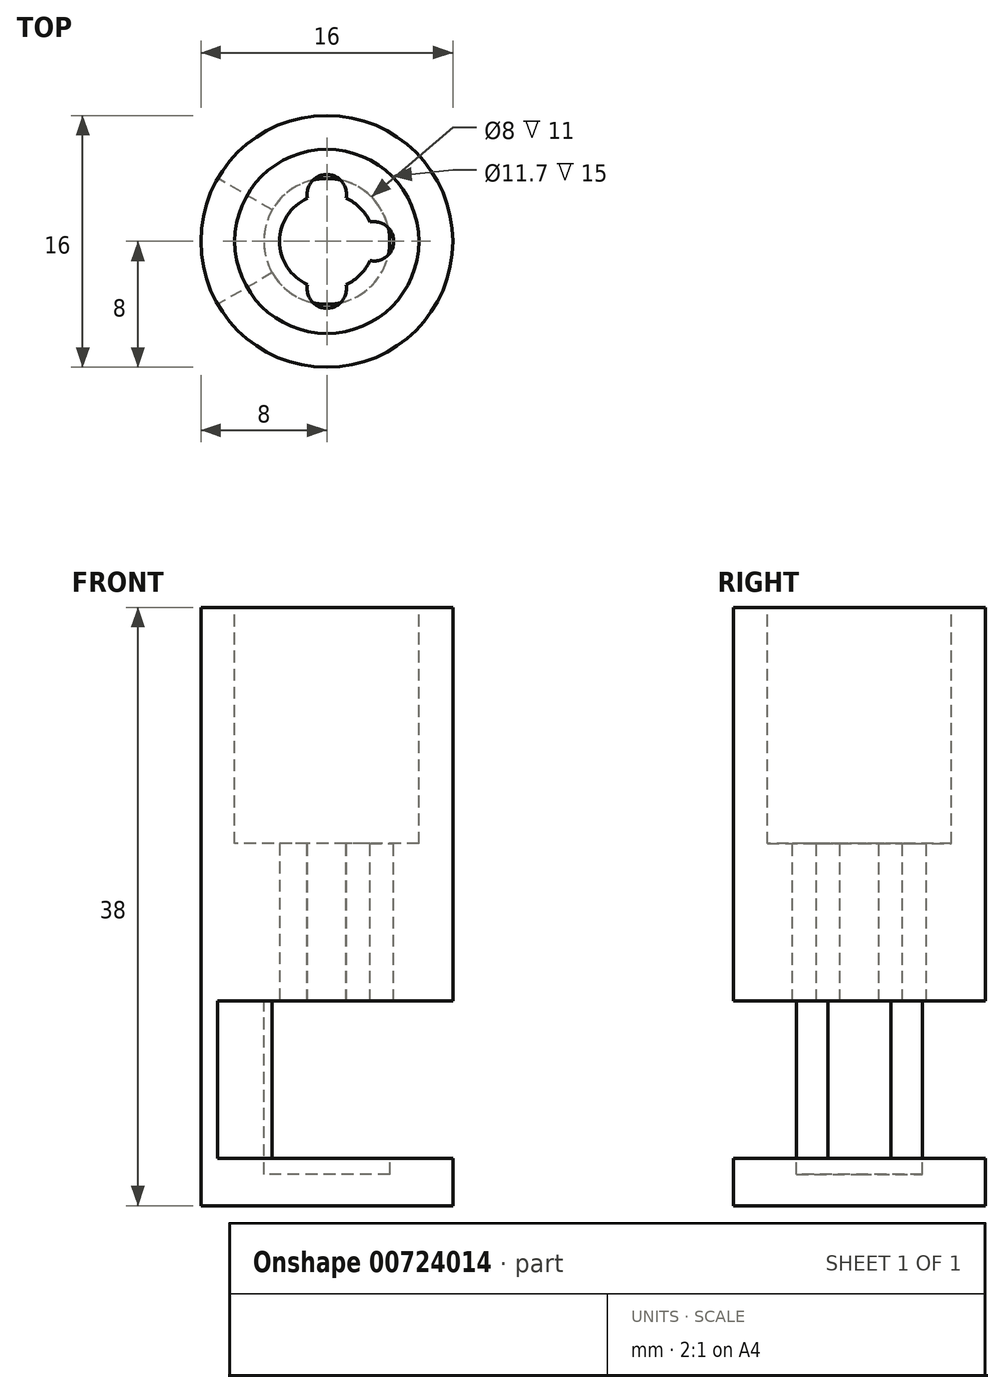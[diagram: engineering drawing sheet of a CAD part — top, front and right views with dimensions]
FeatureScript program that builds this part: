
annotation { "Feature Type Name" : "Feature", "Feature Type Description" : "" }
export const myFeature = defineFeature(function(context is Context, id is Id, definition is map)
    precondition{}
    {
        {
            var Q0;
            Q0=qCreatedBy(makeId("Top.planeOp"),FACE);
            var sketch = newSketch(context, id + "F0", { "sketchPlane" : qUnion([Q0])});
            skCircle(sketch, "E0", {"center": v(0, 0) * mm, "radius": 8 * mm});
            skSolve(sketch);
        }
        {
            var Q0;
            Q0=makeQuery(id+"F0.imprint","IMPRINT",FACE,{"disambiguationData":[TD([[makeQuery(id+"F0.imprint","IMPRINT",EDGE,{"derivedFrom":sQuery(id+"F0.wireOp",EDGE,"E0")}),1.0]])]});
            extrude(context, id + "F1", {"entities" : qUnion([Q0]), "depth" : 3 * mm, "offsetDistance" : 25 * mm});
        }
        {
            var Q0;
            Q0=makeQuery(id+"F1.opExtrude","CAP_FACE",FACE,{"disambiguationData":[OSD([sQuery(id+"F0.wireOp",EDGE,"E0")])],"isStart":false});
            var sketch = newSketch(context, id + "F2", { "sketchPlane" : qUnion([Q0])});
            skCircle(sketch, "E1", {"center": v(0, 0) * mm, "radius": 4 * mm});
            skSolve(sketch);
        }
        {
            var Q0;
            Q0=makeQuery(id+"F2.imprint","IMPRINT",FACE,{"disambiguationData":[TD([[makeQuery(id+"F2.imprint","IMPRINT",EDGE,{"derivedFrom":sQuery(id+"F2.wireOp",EDGE,"E1")}),1.0]])]});
            extrude(context, id + "F3", {"entities" : qUnion([Q0]), "operationType" : NewBodyOperationType.REMOVE, "oppositeDirection" : true, "depth" : 1 * mm, "offsetDistance" : 25 * mm});
        }
        {
            var Q0;
            Q0=makeQuery(id+"F1.opExtrude","CAP_FACE",FACE,{"disambiguationData":[OSD([sQuery(id+"F0.wireOp",EDGE,"E0")])],"isStart":false});
            var sketch = newSketch(context, id + "F4", { "sketchPlane" : qUnion([Q0])});
            skArc(sketch, "E2", {"start": v(-6.93, 4) * mm, "mid": v(-8, 0) * mm, "end": v(-6.93, -4) * mm});
            skLineSegment(sketch, "E3", {"start": v(-3.46, 2) * mm, "end": v(-6.93, 4) * mm});
            skLineSegment(sketch, "E4", {"start": v(-3.46, -2) * mm, "end": v(-6.93, -4) * mm});
            skArc(sketch, "E5", {"start": v(-3.46, 2) * mm, "mid": v(-4, 0) * mm, "end": v(-3.46, -2) * mm});
            skSolve(sketch);
        }
        {
            var Q0;
            Q0=makeQuery(id+"F4.imprint","IMPRINT",FACE,{"disambiguationData":[TD([[makeQuery(id+"F4.imprint","IMPRINT",EDGE,{"derivedFrom":sQuery(id+"F4.wireOp",EDGE,"E2")}),1.0]])]});
            extrude(context, id + "F5", {"entities" : qUnion([Q0]), "operationType" : NewBodyOperationType.ADD, "depth" : 10 * mm, "offsetDistance" : 25 * mm});
        }
        {
            var Q0;
            Q0=makeQuery(id+"F5.opExtrude","CAP_FACE",FACE,{"disambiguationData":[OSD([sQuery(id+"F4.wireOp",EDGE,"E2"),sQuery(id+"F4.wireOp",EDGE,"E3"),sQuery(id+"F4.wireOp",EDGE,"E4"),sQuery(id+"F4.wireOp",EDGE,"E5")])],"isStart":false});
            var sketch = newSketch(context, id + "F6", { "sketchPlane" : qUnion([Q0])});
            skArc(sketch, "E6.0", {"start": v(-6.93, -4) * mm, "mid": v(8, 0) * mm, "end": v(-6.93, 4) * mm});
            skArc(sketch, "E7.0", {"start": v(-6.93, 4) * mm, "mid": v(-8, 0) * mm, "end": v(-6.93, -4) * mm});
            skCircle(sketch, "E8", {"center": v(0, 0) * mm, "radius": 3 * mm});
            skSolve(sketch);
        }
        {
            var Q0;
            Q0=makeQuery(id+"F6.imprint","IMPRINT",FACE,{"disambiguationData":[TD([[makeQuery(id+"F6.imprint","IMPRINT",EDGE,{"derivedFrom":sQuery(id+"F6.wireOp",EDGE,"E6.0")}),1.0]])]});
            var Q1;
            Q1=makeQuery(id+"F6.imprint","IMPRINT",FACE,{"disambiguationData":[TD([[makeQuery(id+"F6.imprint","IMPRINT",EDGE,{"derivedFrom":sQuery(id+"F6.wireOp",EDGE,"E7.0")}),1.0]])]});
            extrude(context, id + "F7", {"entities" : qUnion([Q0, Q1]), "operationType" : NewBodyOperationType.ADD, "depth" : 25 * mm, "offsetDistance" : 25 * mm});
        }
        {
            var Q0;
            Q0=makeQuery(id+"F7.opExtrude","CAP_FACE",FACE,{"disambiguationData":[OSD([sQuery(id+"F6.wireOp",EDGE,"E6.0"),sQuery(id+"F6.wireOp",EDGE,"E7.0"),sQuery(id+"F6.wireOp",EDGE,"E8")])],"isStart":false});
            var sketch = newSketch(context, id + "F8", { "sketchPlane" : qUnion([Q0])});
            skCircle(sketch, "E9", {"center": v(0, 0) * mm, "radius": 5.85 * mm});
            skSolve(sketch);
        }
        {
            var Q0;
            Q0=makeQuery(id+"F8.imprint","IMPRINT",FACE,{"disambiguationData":[TD([[makeQuery(id+"F8.imprint","IMPRINT",EDGE,{"derivedFrom":sQuery(id+"F8.wireOp",EDGE,"E9")}),1.0]])]});
            extrude(context, id + "F9", {"entities" : qUnion([Q0]), "operationType" : NewBodyOperationType.REMOVE, "oppositeDirection" : true, "depth" : 15 * mm, "offsetDistance" : 25 * mm});
        }
        {
            var Q0;
            Q0=makeQuery(id+"F9.boolean.opBoolean","COPY",FACE,{"derivedFrom":makeQuery(id+"F9.opExtrude","CAP_FACE",FACE,{"disambiguationData":[OSD([sQuery(id+"F6.wireOp",EDGE,"E8"),sQuery(id+"F8.wireOp",EDGE,"E9")])],"isStart":false})});
            var sketch = newSketch(context, id + "F10", { "sketchPlane" : qUnion([Q0])});
            skCircle(sketch, "E10", {"center": v(-3, 0) * mm, "radius": 1.25 * mm});
            skCircle(sketch, "E11", {"center": v(0, 3) * mm, "radius": 1.25 * mm});
            skCircle(sketch, "E12", {"center": v(3, 0) * mm, "radius": 1.25 * mm});
            skCircle(sketch, "E13", {"center": v(0, -3) * mm, "radius": 1.25 * mm});
            skSolve(sketch);
        }
        {
            var Q0;
            {var subQ0=sQuery(id+"F10.wireOp",EDGE,"E11");var subQ1=makeQuery(id+"F9.boolean.opBoolean","COPY",EDGE,{"derivedFrom":makeQuery(id+"F9.opExtrude","CAP_EDGE",EDGE,{"disambiguationData":[OSD([sQuery(id+"F6.wireOp",EDGE,"E8")])],"isStart":false})});var subQ2=makeQuery(id+"F10.imprint","INTERSECT",VERTEX,{"disambiguationData":[OD(0.0)],"derivedFrom":[subQ1,subQ0]});Q0=makeQuery(id+"F10.imprint","IMPRINT",FACE,{"disambiguationData":[TD([[makeQuery(id+"F10.imprint","IMPRINT",EDGE,{"disambiguationData":[TD([[subQ2,1.0]])],"derivedFrom":subQ0}),1.0]])]});}
            var Q1;
            {var subQ0=sQuery(id+"F10.wireOp",EDGE,"E12");var subQ1=makeQuery(id+"F9.boolean.opBoolean","COPY",EDGE,{"derivedFrom":makeQuery(id+"F9.opExtrude","CAP_EDGE",EDGE,{"disambiguationData":[OSD([sQuery(id+"F6.wireOp",EDGE,"E8")])],"isStart":false})});var subQ2=makeQuery(id+"F10.imprint","INTERSECT",VERTEX,{"disambiguationData":[OD(0.0)],"derivedFrom":[subQ1,subQ0]});Q1=makeQuery(id+"F10.imprint","IMPRINT",FACE,{"disambiguationData":[TD([[makeQuery(id+"F10.imprint","IMPRINT",EDGE,{"disambiguationData":[TD([[subQ2,-1.0]])],"derivedFrom":subQ0}),1.0]])]});}
            var Q2;
            {var subQ0=sQuery(id+"F10.wireOp",EDGE,"E13");var subQ1=makeQuery(id+"F9.boolean.opBoolean","COPY",EDGE,{"derivedFrom":makeQuery(id+"F9.opExtrude","CAP_EDGE",EDGE,{"disambiguationData":[OSD([sQuery(id+"F6.wireOp",EDGE,"E8")])],"isStart":false})});var subQ2=makeQuery(id+"F10.imprint","INTERSECT",VERTEX,{"disambiguationData":[OD(0.0)],"derivedFrom":[subQ1,subQ0]});Q2=makeQuery(id+"F10.imprint","IMPRINT",FACE,{"disambiguationData":[TD([[makeQuery(id+"F10.imprint","IMPRINT",EDGE,{"disambiguationData":[TD([[subQ2,-1.0]])],"derivedFrom":subQ0}),1.0]])]});}
            extrude(context, id + "F11", {"entities" : qUnion([Q0, Q1, Q2]), "operationType" : NewBodyOperationType.REMOVE, "endBound" : BoundingType.UP_TO_NEXT, "oppositeDirection" : true, "depth" : 25 * mm, "offsetDistance" : 25 * mm});
        }
    });
